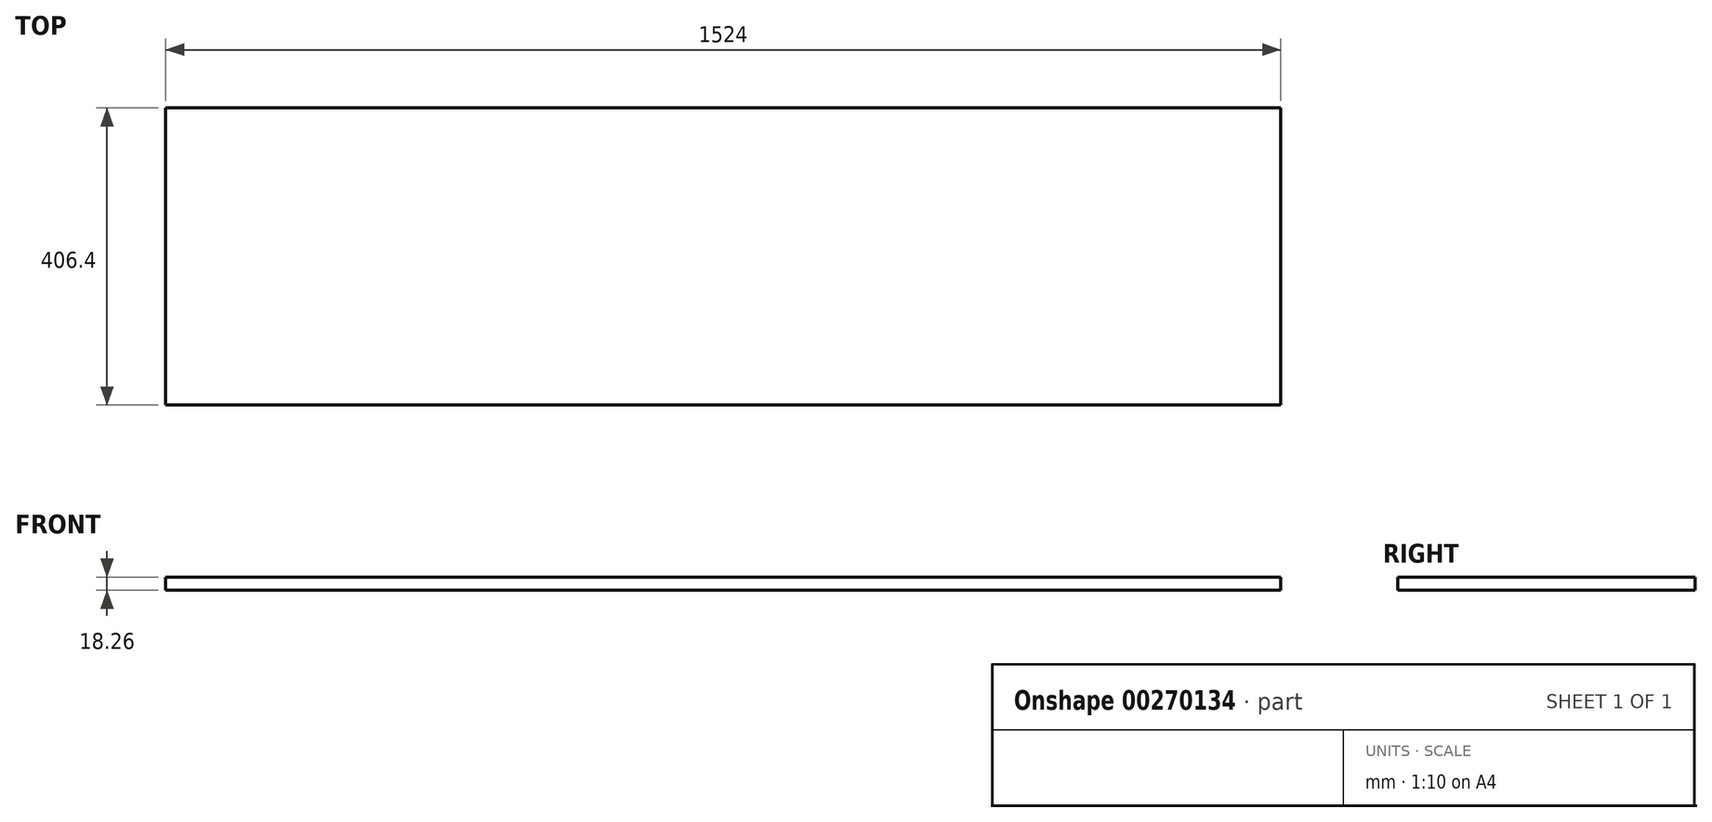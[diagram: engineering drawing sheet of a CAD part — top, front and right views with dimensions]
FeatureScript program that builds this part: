
annotation { "Feature Type Name" : "Feature", "Feature Type Description" : "" }
export const myFeature = defineFeature(function(context is Context, id is Id, definition is map)
    precondition{}
    {
        {
            var Q0;
            Q0=qCreatedBy(makeId("Top.planeOp"),FACE);
            var sketch = newSketch(context, id + "F0", { "sketchPlane" : qUnion([Q0])});
            skLineSegment(sketch, "E0.bottom", {"start": v(762, -203.2) * mm, "end": v(-762, -203.2) * mm});
            skLineSegment(sketch, "E0.top", {"start": v(762, 203.2) * mm, "end": v(-762, 203.2) * mm});
            skLineSegment(sketch, "E0.left", {"start": v(762, -203.2) * mm, "end": v(762, 203.2) * mm});
            skLineSegment(sketch, "E0.right", {"start": v(-762, -203.2) * mm, "end": v(-762, 203.2) * mm});
            skPoint(sketch, "E0.middle", {"position": v(0, 0) * mm});
            skSolve(sketch);
        }
        {
            var Q0;
            Q0=makeQuery(id+"F0.imprint","IMPRINT",FACE,{"disambiguationData":[TD([[makeQuery(id+"F0.imprint","IMPRINT",EDGE,{"derivedFrom":sQuery(id+"F0.wireOp",EDGE,"E0.bottom")}),-1.0]])]});
            extrude(context, id + "F1", {"entities" : qUnion([Q0]), "depth" : 18.26 * mm});
        }
    });
